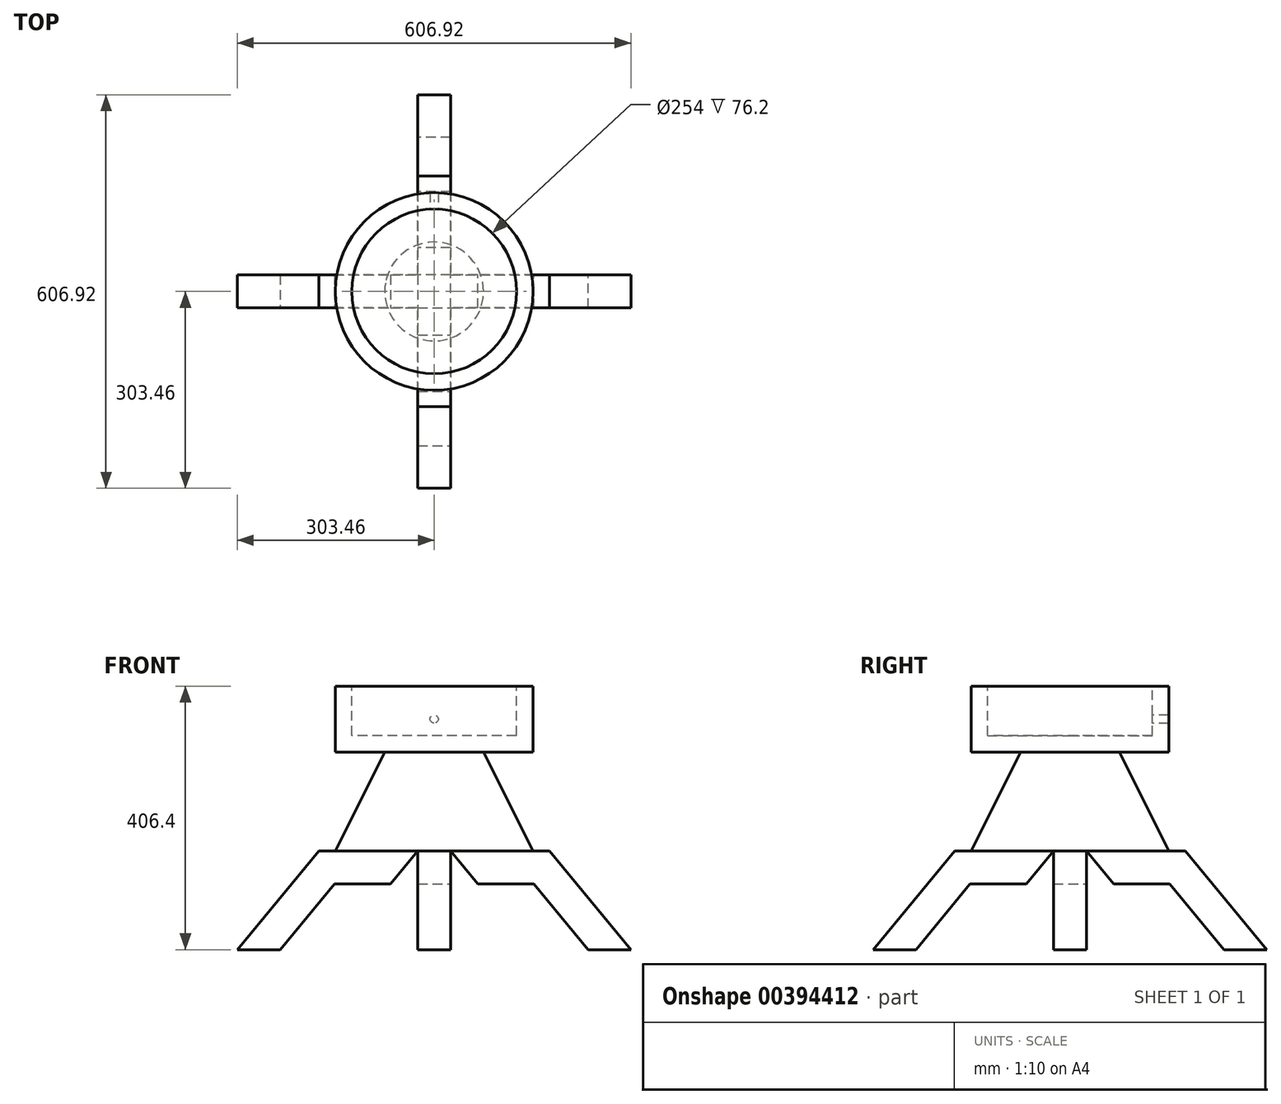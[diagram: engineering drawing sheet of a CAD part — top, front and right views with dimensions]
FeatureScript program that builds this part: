
annotation { "Feature Type Name" : "Feature", "Feature Type Description" : "" }
export const myFeature = defineFeature(function(context is Context, id is Id, definition is map)
    precondition{}
    {
        {
            var Q0;
            Q0=qCreatedBy(makeId("Front.planeOp"),FACE);
            var sketch = newSketch(context, id + "F0", { "sketchPlane" : qUnion([Q0])});
            skLineSegment(sketch, "E0", {"start": v(0, 0) * mm, "end": v(-152.4, 0) * mm});
            skLineSegment(sketch, "E1", {"start": v(-152.4, 0) * mm, "end": v(-76.2, 152.4) * mm});
            skLineSegment(sketch, "E2", {"start": v(-76.2, 152.4) * mm, "end": v(0, 152.4) * mm});
            skLineSegment(sketch, "E3", {"start": v(0, 152.4) * mm, "end": v(0, 0) * mm});
            skLineSegment(sketch, "E4", {"start": v(0, 152.4) * mm, "end": v(-152.4, 152.4) * mm});
            skLineSegment(sketch, "E5", {"start": v(-152.4, 152.4) * mm, "end": v(-152.4, 254) * mm});
            skLineSegment(sketch, "E6", {"start": v(-152.4, 254) * mm, "end": v(-127, 254) * mm});
            skLineSegment(sketch, "E7", {"start": v(-127, 254) * mm, "end": v(-127, 177.8) * mm});
            skLineSegment(sketch, "E8", {"start": v(-127, 177.8) * mm, "end": v(0, 177.8) * mm});
            skLineSegment(sketch, "E9", {"start": v(0, 177.8) * mm, "end": v(0, 152.4) * mm});
            skSolve(sketch);
        }
        {
            var Q0;
            {var subQ0=sQuery(id+"F0.wireOp",EDGE,"E5");Q0=makeQuery(id+"F0.imprint","IMPRINT",FACE,{"disambiguationData":[TD([[makeQuery(id+"F0.imprint","IMPRINT",EDGE,{"derivedFrom":subQ0}),-1.0]])]});}
            var Q1;
            Q1=makeQuery(id+"F0.imprint","IMPRINT",FACE,{"disambiguationData":[TD([[makeQuery(id+"F0.imprint","IMPRINT",EDGE,{"derivedFrom":sQuery(id+"F0.wireOp",EDGE,"E0")}),-1.0]])]});
            var Q2;
            Q2=sQuery(id+"F0.wireOp",EDGE,"E3");
            revolve(context, id + "F1", {"entities" : qUnion([Q0, Q1]), "axis" : qUnion([Q2]), "revolveType" : RevolveType.FULL});
        }
        {
            var Q0;
            Q0=qCreatedBy(makeId("Front.planeOp"),FACE);
            var sketch = newSketch(context, id + "F2", { "sketchPlane" : qUnion([Q0])});
            skLineSegment(sketch, "E10", {"start": v(0, 0) * mm, "end": v(25.4, 0) * mm});
            skLineSegment(sketch, "E11", {"start": v(25.4, 0) * mm, "end": v(177.8, 0) * mm});
            skLineSegment(sketch, "E12", {"start": v(177.8, 0) * mm, "end": v(303.46, -152.4) * mm});
            skLineSegment(sketch, "E13", {"start": v(303.46, -152.4) * mm, "end": v(237.62, -152.4) * mm});
            skLineSegment(sketch, "E14", {"start": v(237.62, -152.4) * mm, "end": v(153.84, -50.8) * mm});
            skLineSegment(sketch, "E15", {"start": v(153.84, -50.8) * mm, "end": v(67.29, -50.8) * mm});
            skLineSegment(sketch, "E16", {"start": v(67.29, -50.8) * mm, "end": v(25.4, 0) * mm});
            skSolve(sketch);
        }
        {
            var Q0;
            Q0=makeQuery(id+"F2.imprint","IMPRINT",FACE,{"disambiguationData":[TD([[makeQuery(id+"F2.imprint","IMPRINT",EDGE,{"derivedFrom":sQuery(id+"F2.wireOp",EDGE,"E11")}),-1.0]])]});
            extrude(context, id + "F3", {"entities" : qUnion([Q0]), "operationType" : NewBodyOperationType.ADD, "endBound" : BoundingType.SYMMETRIC, "depth" : 50.8 * mm});
        }
        {
            var Q0;
            Q0=makeQuery(id+"F1.opRevolve","SWEPT_BODY",BODY,{"disambiguationData":[OSD([sQuery(id+"F0.wireOp",EDGE,"E0"),sQuery(id+"F0.wireOp",EDGE,"E1"),sQuery(id+"F0.wireOp",EDGE,"E3"),sQuery(id+"F0.wireOp",EDGE,"E4"),sQuery(id+"F0.wireOp",EDGE,"E5"),sQuery(id+"F0.wireOp",EDGE,"E6"),sQuery(id+"F0.wireOp",EDGE,"E7"),sQuery(id+"F0.wireOp",EDGE,"E8"),sQuery(id+"F0.wireOp",EDGE,"E9")])]});
            var Q1;
            Q1=makeQuery(id+"F1.opRevolve","SWEPT_FACE",FACE,{"disambiguationData":[OSD([sQuery(id+"F0.wireOp",EDGE,"E1")])]});
            circularPattern(context, id + "F4", {"operationType" : NewBodyOperationType.ADD, "entities" : qUnion([Q0]), "axis" : qUnion([Q1]), "angle" : 360 * degree, "instanceCount" : 4, "equalSpace" : true});
        }
        {
            var Q0;
            Q0=qCreatedBy(makeId("Front.planeOp"),FACE);
            var sketch = newSketch(context, id + "F5", { "sketchPlane" : qUnion([Q0])});
            skCircle(sketch, "E17", {"center": v(0, 203.2) * mm, "radius": 6.35 * mm});
            skSolve(sketch);
        }
        {
            var Q0;
            Q0 = qSketchRegion(id + "F5", true);
            extrude(context, id + "F6", {"entities" : qUnion([Q0]), "operationType" : NewBodyOperationType.REMOVE, "oppositeDirection" : true, "depth" : 508 * mm});
        }
    });
